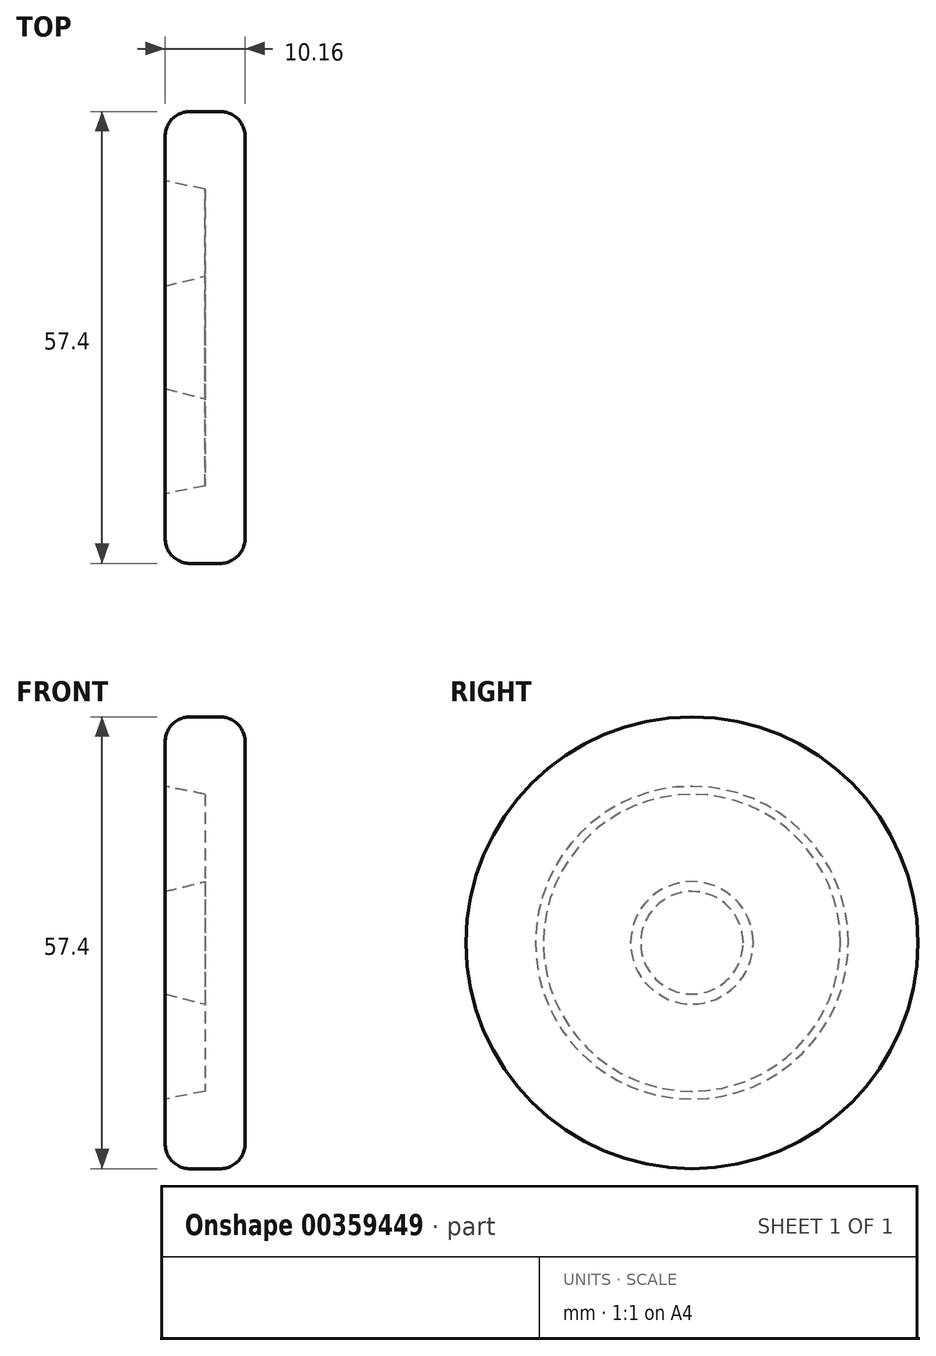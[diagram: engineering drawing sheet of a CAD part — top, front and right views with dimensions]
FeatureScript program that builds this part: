
annotation { "Feature Type Name" : "Feature", "Feature Type Description" : "" }
export const myFeature = defineFeature(function(context is Context, id is Id, definition is map)
    precondition{}
    {
        {
            var Q0;
            Q0=qCreatedBy(makeId("Front.planeOp"),FACE);
            var sketch = newSketch(context, id + "F0", { "sketchPlane" : qUnion([Q0])});
            skLineSegment(sketch, "E0", {"start": v(-4.4, 0) * mm, "end": v(5.76, 0) * mm});
            skLineSegment(sketch, "E1", {"start": v(-4.4, 0) * mm, "end": v(-4.4, 25.53) * mm});
            skLineSegment(sketch, "E2", {"start": v(-1.23, 28.7) * mm, "end": v(2.58, 28.7) * mm});
            skLineSegment(sketch, "E3", {"start": v(5.76, 25.53) * mm, "end": v(5.76, 0) * mm});
            skPoint(sketch, "E4.visualSharp", {"position": v(-4.4, 28.7) * mm});
            skArc(sketch, "E4.filletArc", {"start": v(-3.89, 28.7) * mm, "mid": v(-3.95, 28.7) * mm, "end": v(-4, 28.69) * mm});
            skArc(sketch, "E5.filletArc", {"start": v(-1.23, 28.7) * mm, "mid": v(-3.47, 27.77) * mm, "end": v(-4.4, 25.53) * mm});
            skPoint(sketch, "E6.visualSharp", {"position": v(5.76, 28.7) * mm});
            skArc(sketch, "E6.filletArc", {"start": v(5.76, 25.53) * mm, "mid": v(4.83, 27.77) * mm, "end": v(2.58, 28.7) * mm});
            skLineSegment(sketch, "E7", {"start": v(0.68, 18.86) * mm, "end": v(0.68, 7.78) * mm});
            skLineSegment(sketch, "E8", {"start": v(0.68, 7.78) * mm, "end": v(-4.4, 6.51) * mm});
            skLineSegment(sketch, "E9", {"start": v(-4.4, 19.87) * mm, "end": v(0.68, 18.86) * mm});
            skLineSegment(sketch, "E10", {"start": v(0.68, 16) * mm, "end": v(5.76, 16) * mm});
            skLineSegment(sketch, "E11", {"start": v(0.68, 9.4) * mm, "end": v(5.76, 9.4) * mm});
            skSolve(sketch);
        }
        {
            var Q0;
            {var subQ0=sQuery(id+"F0.wireOp",EDGE,"E10");Q0=makeQuery(id+"F0.imprint","IMPRINT",FACE,{"disambiguationData":[TD([[makeQuery(id+"F0.imprint","IMPRINT",EDGE,{"derivedFrom":subQ0}),-1.0]])]});}
            var Q1;
            Q1=makeQuery(id+"F0.imprint","IMPRINT",FACE,{"disambiguationData":[TD([[makeQuery(id+"F0.imprint","IMPRINT",EDGE,{"derivedFrom":sQuery(id+"F0.wireOp",EDGE,"E2")}),-1.0]])]});
            var Q2;
            {var subQ4=sQuery(id+"F0.wireOp",EDGE,"E0");Q2=makeQuery(id+"F0.imprint","IMPRINT",FACE,{"disambiguationData":[TD([[makeQuery(id+"F0.imprint","IMPRINT",EDGE,{"derivedFrom":subQ4}),1.0]])]});}
            var Q3;
            Q3=sQuery(id+"F0.wireOp",EDGE,"E0");
            revolve(context, id + "F1", {"surfaceOperationType" : NewSurfaceOperationType.ADD, "entities" : qUnion([Q0, Q1, Q2]), "axis" : qUnion([Q3]), "revolveType" : RevolveType.FULL});
        }
    });
